# Revit family: Damper-Cable_Operated-Carnes-Rectangular-Opposed_Blade_FQAA
name_source: partatom
category: Duct Accessories
revit_build: Autodesk Revit Architecture 2012 (Build: 20110916_2132(x64)
units: mm (PartAtom-declared; Revit-internal decimal feet)

## types (1)
- FQAA
    04 CSI = 08 91 00
    95 CSI = 10200
    Assembly Code = D3090700
    Blade Material = Aluminum - Carnes - Extruded
    Catalog URL = http://www.carnes.com
    Connector Description 1 = Duct Connection 1
    Connector Description 2 = Duct Connection 2
    Controller Height = 8"
    Controller Length = 4"
    Controller Offset = 3"
    Controller Width = 1 1/2"
    Damper Air Flow = 0 CFM
    Description = Cable Operated Dampers
    Frame Material = Aluminum - Carnes - Extruded
    Manufacturer = Carnes Company
    Manufacturer Fax = 608-845-6470
    Model = FQAA
    Pressure Drop = 0.00 Pa
    Product Line = Cable Operated Dampers
    Product Page URL = http://www.carnes.com
    Specifications  URL = http://www.carnes.com
    Subcategory = Louvers and Dampers
    URL = http://www.carnes.com
    ecoScorecard Product Page = http://ecoscorecard.com

## geometry (parser evidence)
native form markers: Blend x2, Sweep x3
no freeform markers — native parametric forms only
